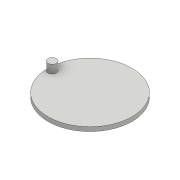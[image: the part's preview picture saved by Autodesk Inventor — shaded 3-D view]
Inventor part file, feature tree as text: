
AUTODESK INVENTOR PART (.ipt)
format: ipt  version: 2017 (Build 210142000, 142)  size: 82,432 bytes
history: native  units: mm
features: extrude x2, sketch x2
ambient origin geometry x8: Origin, YZ Plane, XZ Plane, XY Plane, X Axis, Y Axis, Z Axis, Center Point
bodies: Solid1 (feature_tree)
feature tree (4):
  extrude  "Extrusion1"  Depth=5.0mm TaperAngle=0.0deg
  extrude  "Extrusion2"  [1 undecoded]
  sketch  "Sketch1"  dims[d0=100.0mm d1=5.0mm d2=0.0mm]
  sketch  "Sketch2"  dims[d4=10.0mm d5=0.0mm]
note: 1 required parameter value undecoded (feature->parameter linkage not recoverable at this tier; creation-order binding heuristic only, values carry confidence <= 0.55)
